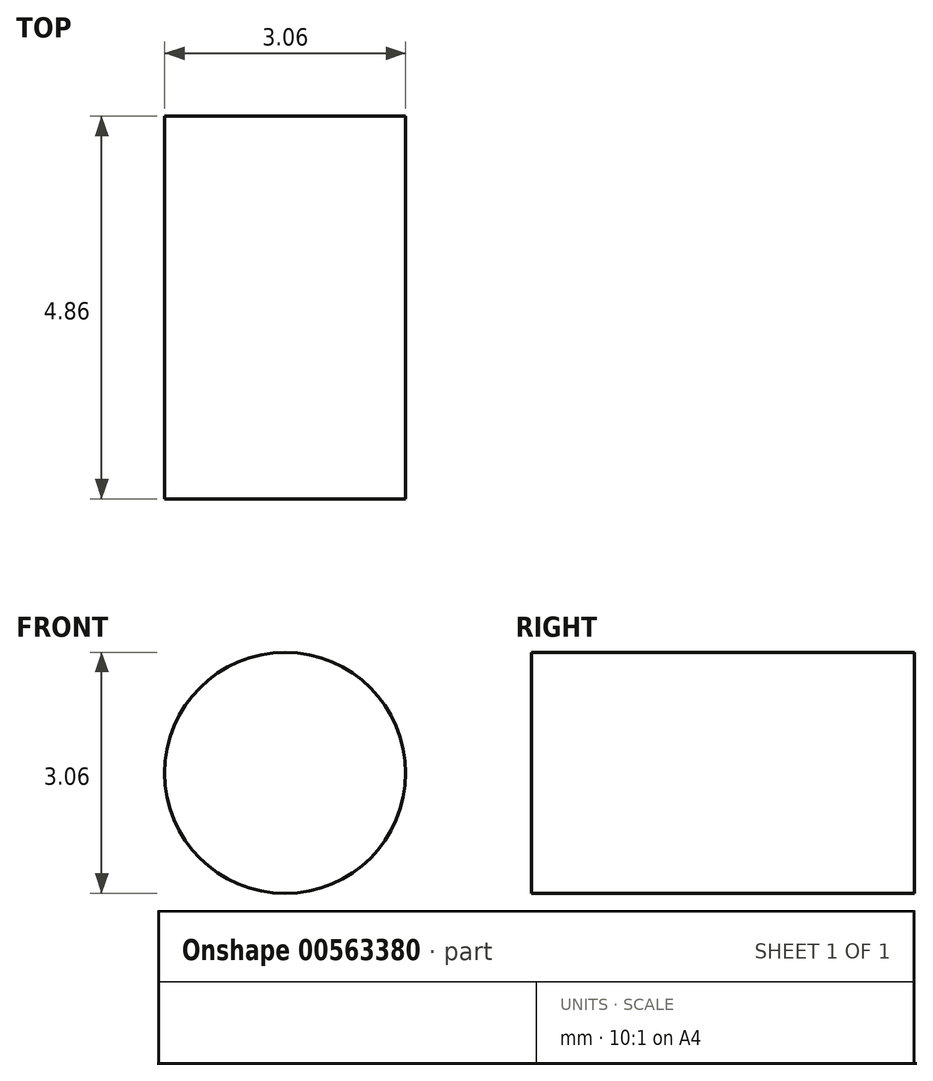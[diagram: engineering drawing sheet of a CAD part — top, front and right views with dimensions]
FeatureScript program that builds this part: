
annotation { "Feature Type Name" : "Feature", "Feature Type Description" : "" }
export const myFeature = defineFeature(function(context is Context, id is Id, definition is map)
    precondition{}
    {
        {
            var Q0;
            Q0=qCreatedBy(makeId("Front.planeOp"),FACE);
            var sketch = newSketch(context, id + "F0", { "sketchPlane" : qUnion([Q0])});
            skCircle(sketch, "E0", {"center": v(-51.77, 41.22) * mm, "radius": 1.53 * mm});
            skSolve(sketch);
        }
        {
            var Q0;
            Q0=qSketchRegion(id+"F0",true);
            extrude(context, id + "F1", {"entities" : qUnion([Q0]), "depth" : 4.86 * mm});
        }
    });
